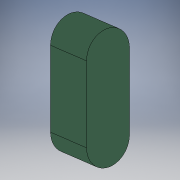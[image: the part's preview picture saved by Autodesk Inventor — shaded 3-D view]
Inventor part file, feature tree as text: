
AUTODESK INVENTOR PART (.ipt)
format: ipt  version: 2018 (Build 220112000, 112)  size: 95,232 bytes
history: native  units: mm
features: extrude x1, sketch x1
ambient origin geometry x8: Origin, YZ Plane, XZ Plane, XY Plane, X Axis, Y Axis, Z Axis, Center Point
bodies: Solid1 (feature_tree)
feature tree (2):
  extrude  "Extrusion1"  Depth=3.0mm
  sketch  "Sketch1"  dims[d0=1.5mm d1=5.0mm d2=3.0mm d3=0.0mm]
